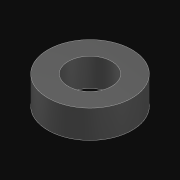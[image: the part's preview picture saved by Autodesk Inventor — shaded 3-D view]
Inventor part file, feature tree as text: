
AUTODESK INVENTOR PART (.ipt)
format: ipt  version: 2021.3 (Build 253353010, 353A)  size: 113,664 bytes
history: native  units: in
note: dims shown in document units (in); Inventor stores cm internally (conversion verified against a paired STEP export)
features: other x5, extrude x1, sketch x1
ambient origin geometry x8: Origin, YZ Plane, XZ Plane, XY Plane, X Axis, Y Axis, Z Axis, Center Point
bodies: Solid1 (feature_tree)
feature tree (7):
  other  "Table"
  other  "NSpacer .375 OD x .125"
  other  "NSpacer .375 OD x .250"
  other  "NSpacer .375 OD x .375"
  other  "NSpacer .375 OD x .500"
  extrude  "Extrusion1"  Depth=0.375in
  sketch  "Sketch1"  dims[d0=0.194in d1=0.375in d3=0.0in]
